# Revit family: STI-102 IP телефон_RV17_LOD400
name_source: partatom
category: Телефонные устройства
revit_build: Autodesk Revit 2017 (Build: 20170118_1100(x64)
units: mm (PartAtom-declared; Revit-internal decimal feet)

## family parameters
Всегда вертикально = Нет
На основе рабочей плоскости = Нет
Общий = Нет
При загрузке вырезать с полостями = Нет
Размер круглого соединителя = Использовать диаметр
Сохранять ориентацию аннотаций = Нет
Тип детали = Нормальный
Точка расчета площади = Нет

## types (1)
- STI-102 IP телефон
    ADSK_URL страницы изделия = https://stilsoft.ru
    ADSK_Единица измерения = шт.
    ADSK_Завод-изготовитель = ООО «Основа Безопасности»
    ADSK_Количество = 1
    ADSK_Марка = СТВФ.431295.007
    ADSK_Масса = 1
    ADSK_Наименование = IP телефон STI-102
    ADSK_Размер_Высота = 287 мм
    ADSK_Размер_Глубина = 121 мм
    ADSK_Размер_Ширина = 157 мм
    d_короба = 20 мм
    Диапазон напряжения электропитания постоянного тока, В = 12-24 (Passive РоЕ)
    Диапазон рабочих температур, <unrecoverable-encoding: 5 bytes ef82b0d0a1> = от -40 до +50
    Интерфейс связи = 10BaseT/100Base TX Ethernet
    Исполнение = Уличное
    Класс защиты = IP65
    Потребляемый ток при 12В / 24В, А = 0,6 / 0,2
    Режим работы = непрерывный
